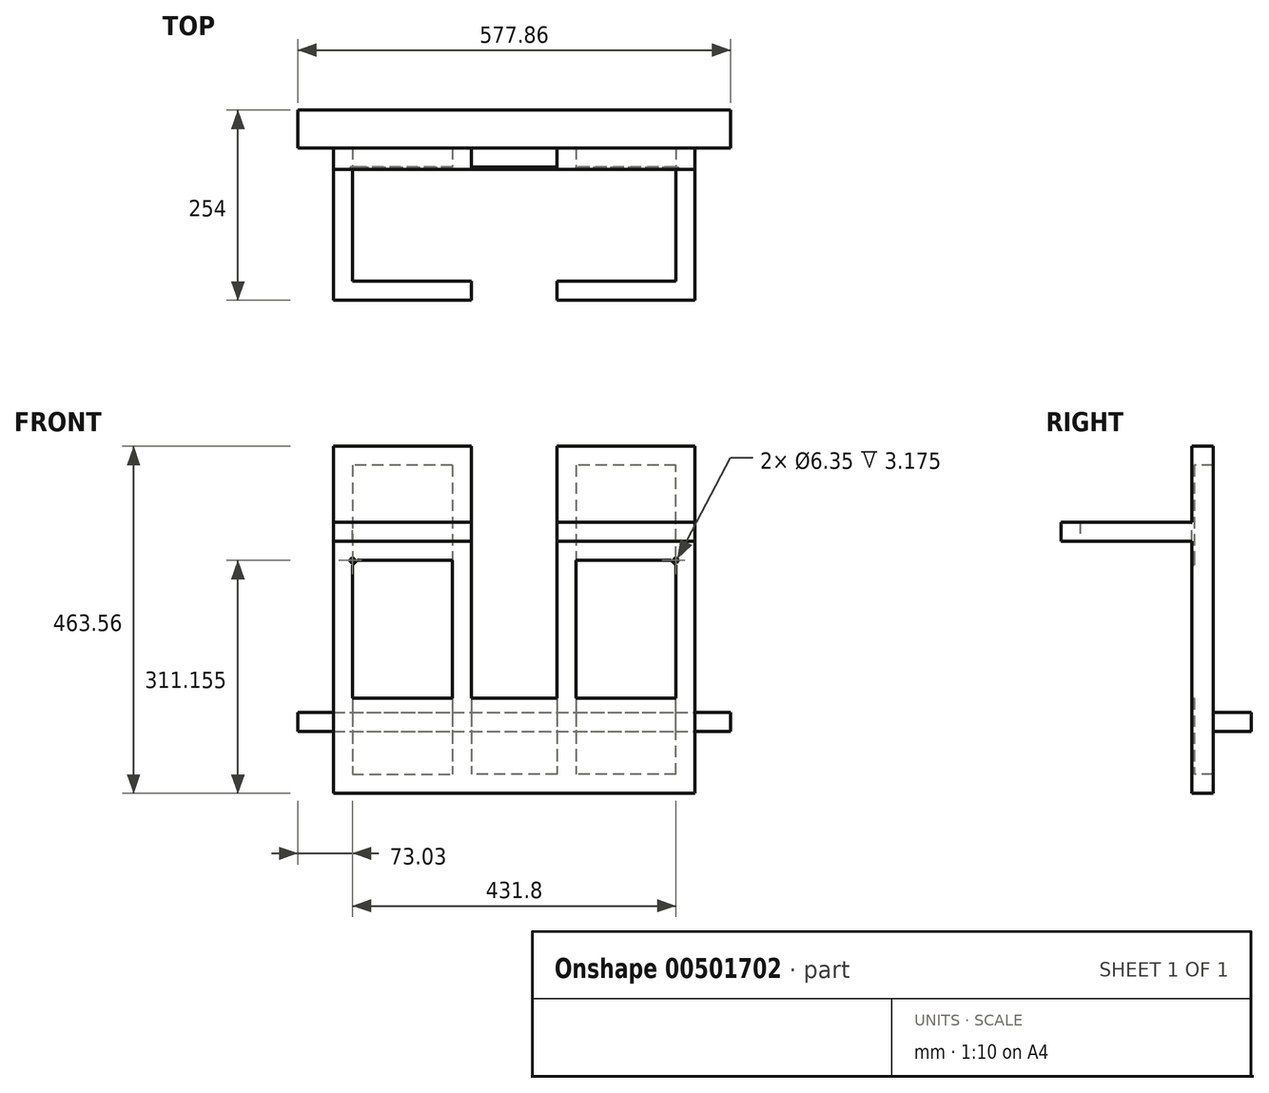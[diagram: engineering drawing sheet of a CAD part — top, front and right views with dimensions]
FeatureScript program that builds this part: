
annotation { "Feature Type Name" : "Feature", "Feature Type Description" : "" }
export const myFeature = defineFeature(function(context is Context, id is Id, definition is map)
    precondition{}
    {
        {
            var Q0;
            Q0=qCreatedBy(makeId("Front.planeOp"),FACE);
            var sketch = newSketch(context, id + "F0", { "sketchPlane" : qUnion([Q0])});
            skLineSegment(sketch, "E0.top", {"start": v(241.3, 231.78) * mm, "end": v(57.15, 231.78) * mm});
            skLineSegment(sketch, "E0.left", {"start": v(241.3, -231.78) * mm, "end": v(241.3, 231.78) * mm});
            skLineSegment(sketch, "E0.right", {"start": v(-241.3, -231.78) * mm, "end": v(-241.3, 231.77) * mm});
            skPoint(sketch, "E0.middle", {"position": v(0, 0) * mm});
            skLineSegment(sketch, "E1", {"start": v(-241.3, 231.77) * mm, "end": v(-57.15, 231.77) * mm});
            skLineSegment(sketch, "E2.trimOffspring", {"start": v(-57.15, 231.78) * mm, "end": v(-241.3, 231.77) * mm});
            skLineSegment(sketch, "E3", {"start": v(-241.3, 231.77) * mm, "end": v(-241.3, 79.37) * mm});
            skLineSegment(sketch, "E4", {"start": v(-209.55, 79.37) * mm, "end": v(-82.55, 79.37) * mm});
            skLineSegment(sketch, "E5", {"start": v(82.55, 79.37) * mm, "end": v(209.55, 79.37) * mm});
            skLineSegment(sketch, "E6", {"start": v(-82.55, 79.37) * mm, "end": v(-82.55, -104.78) * mm});
            skLineSegment(sketch, "E7", {"start": v(-215.9, 73.02) * mm, "end": v(-215.9, -104.78) * mm});
            skLineSegment(sketch, "E8", {"start": v(215.9, -104.78) * mm, "end": v(215.9, 73.02) * mm});
            skLineSegment(sketch, "E9", {"start": v(-241.3, -231.78) * mm, "end": v(241.3, -231.78) * mm});
            skLineSegment(sketch, "E10", {"start": v(-57.15, 231.77) * mm, "end": v(-57.15, -104.78) * mm});
            skLineSegment(sketch, "E11", {"start": v(57.15, 231.78) * mm, "end": v(57.15, -104.78) * mm});
            skLineSegment(sketch, "E12", {"start": v(82.55, -104.78) * mm, "end": v(82.55, 79.37) * mm});
            skLineSegment(sketch, "E13", {"start": v(-241.3, -231.78) * mm, "end": v(-241.3, -104.78) * mm});
            skLineSegment(sketch, "E14", {"start": v(-215.9, -104.78) * mm, "end": v(-82.55, -104.78) * mm});
            skLineSegment(sketch, "E15.trimOffspring", {"start": v(-57.15, -104.78) * mm, "end": v(57.15, -104.78) * mm});
            skLineSegment(sketch, "E16.trimOffspring", {"start": v(82.55, -104.78) * mm, "end": v(215.9, -104.78) * mm});
            skLineSegment(sketch, "E17", {"start": v(-209.55, 79.37) * mm, "end": v(-215.9, 73.02) * mm});
            skLineSegment(sketch, "E18", {"start": v(215.9, 73.02) * mm, "end": v(209.55, 79.37) * mm});
            skSolve(sketch);
        }
        {
            var Q0;
            Q0 = qSketchRegion(id + "F0", true);
            extrude(context, id + "F1", {"entities" : qUnion([Q0]), "depth" : 3.17 * mm});
        }
        {
            var Q0;
            Q0=makeQuery(id+"F1.opExtrude","SWEPT_FACE",FACE,{"disambiguationData":[OSD([sQuery(id+"F0.wireOp",EDGE,"E0.left")])]});
            var sketch = newSketch(context, id + "F2", { "sketchPlane" : qUnion([Q0])});
            skLineSegment(sketch, "E19", {"start": v(0, 130.18) * mm, "end": v(-177.8, 130.18) * mm});
            skLineSegment(sketch, "E20", {"start": v(-177.8, 130.18) * mm, "end": v(-177.8, 104.78) * mm});
            skLineSegment(sketch, "E21", {"start": v(-177.8, 104.78) * mm, "end": v(0, 104.78) * mm});
            skLineSegment(sketch, "E22", {"start": v(0, 104.78) * mm, "end": v(0, 130.18) * mm});
            skSolve(sketch);
        }
        {
            var Q0;
            Q0 = qSketchRegion(id + "F2", true);
            extrude(context, id + "F3", {"entities" : qUnion([Q0]), "operationType" : NewBodyOperationType.ADD, "oppositeDirection" : true, "depth" : 25.4 * mm});
        }
        {
            var Q0;
            Q0=makeQuery(id+"F3.opExtrude","SWEPT_FACE",FACE,{"disambiguationData":[OSD([sQuery(id+"F2.wireOp",EDGE,"E20")])]});
            var sketch = newSketch(context, id + "F4", { "sketchPlane" : qUnion([Q0])});
            skLineSegment(sketch, "E23", {"start": v(241.3, 130.18) * mm, "end": v(57.15, 130.18) * mm});
            skLineSegment(sketch, "E24", {"start": v(57.15, 130.18) * mm, "end": v(57.15, 104.78) * mm});
            skLineSegment(sketch, "E25", {"start": v(57.15, 104.78) * mm, "end": v(241.3, 104.78) * mm});
            skLineSegment(sketch, "E26", {"start": v(241.3, 130.18) * mm, "end": v(241.3, 104.78) * mm});
            skSolve(sketch);
        }
        {
            var Q0;
            Q0 = qSketchRegion(id + "F4", true);
            extrude(context, id + "F5", {"entities" : qUnion([Q0]), "operationType" : NewBodyOperationType.ADD, "oppositeDirection" : true, "depth" : 25.4 * mm});
        }
        {
            var Q0;
            Q0=makeQuery(id+"F1.opExtrude","SWEPT_BODY",BODY,{"disambiguationData":[OSD([sQuery(id+"F0.wireOp",EDGE,"E0.bottom"),sQuery(id+"F0.wireOp",EDGE,"E0.left"),sQuery(id+"F0.wireOp",EDGE,"E0.right"),sQuery(id+"F0.wireOp",EDGE,"E0.top"),sQuery(id+"F0.wireOp",EDGE,"z7k5WuwH-fP3U-BbjL-vrnD-IwZhUuzp3tKr"),sQuery(id+"F0.wireOp",EDGE,"sfKOh3xY-R45W-dPWh-zpq8-PP8cvFYOitUN"),sQuery(id+"F0.wireOp",EDGE,"E2.trimOffspring"),sQuery(id+"F0.wireOp",EDGE,"tUk4NjoC-bmQa-DXwl-oMC2-rkoS1IceVBJg")])]});
            var Q1;
            Q1=qCreatedBy(makeId("Right.planeOp"),FACE);
            mirror(context, id + "F6", {"operationType" : NewBodyOperationType.ADD, "entities" : qUnion([Q0]), "mirrorPlane" : qUnion([Q1])});
        }
        {
            var Q0;
            Q0=makeQuery(id+"F1.opExtrude","CAP_FACE",FACE,{"disambiguationData":[OSD([sQuery(id+"F0.wireOp",EDGE,"E0.bottom"),sQuery(id+"F0.wireOp",EDGE,"E0.left"),sQuery(id+"F0.wireOp",EDGE,"E0.right"),sQuery(id+"F0.wireOp",EDGE,"E0.top"),sQuery(id+"F0.wireOp",EDGE,"z7k5WuwH-fP3U-BbjL-vrnD-IwZhUuzp3tKr"),sQuery(id+"F0.wireOp",EDGE,"sfKOh3xY-R45W-dPWh-zpq8-PP8cvFYOitUN"),sQuery(id+"F0.wireOp",EDGE,"E2.trimOffspring"),sQuery(id+"F0.wireOp",EDGE,"tUk4NjoC-bmQa-DXwl-oMC2-rkoS1IceVBJg")])],"isStart":false});
            var sketch = newSketch(context, id + "F7", { "sketchPlane" : qUnion([Q0])});
            skLineSegment(sketch, "E27.top", {"start": v(107.95, 215.44) * mm, "end": v(-107.95, 215.44) * mm});
            skPoint(sketch, "E27.middle", {"position": v(0, 0) * mm});
            skPoint(sketch, "E27.left.start.orphan", {"position": v(107.95, -215.44) * mm});
            skPoint(sketch, "E27.right.start.orphan", {"position": v(-107.95, -215.44) * mm});
            skCircle(sketch, "E28", {"center": v(-215.9, 79.38) * mm, "radius": 3.18 * mm});
            skCircle(sketch, "E29.MirrorC", {"center": v(215.9, 79.38) * mm, "radius": 3.18 * mm});
            skSolve(sketch);
        }
        {
            var Q0;
            Q0 = qSketchRegion(id + "F7", true);
            extrude(context, id + "F8", {"entities" : qUnion([Q0]), "operationType" : NewBodyOperationType.REMOVE, "oppositeDirection" : true, "depth" : 25.4 * mm});
        }
        {
            var Q0;
            Q0=makeQuery(id+"F1.opExtrude","CAP_FACE",FACE,{"disambiguationData":[OSD([sQuery(id+"F0.wireOp",EDGE,"E0.bottom"),sQuery(id+"F0.wireOp",EDGE,"E0.left"),sQuery(id+"F0.wireOp",EDGE,"E0.right"),sQuery(id+"F0.wireOp",EDGE,"E0.top"),sQuery(id+"F0.wireOp",EDGE,"z7k5WuwH-fP3U-BbjL-vrnD-IwZhUuzp3tKr"),sQuery(id+"F0.wireOp",EDGE,"sfKOh3xY-R45W-dPWh-zpq8-PP8cvFYOitUN"),sQuery(id+"F0.wireOp",EDGE,"E2.trimOffspring"),sQuery(id+"F0.wireOp",EDGE,"tUk4NjoC-bmQa-DXwl-oMC2-rkoS1IceVBJg")])],"isStart":true});
            var sketch = newSketch(context, id + "F9", { "sketchPlane" : qUnion([Q0])});
            skLineSegment(sketch, "E30", {"start": v(-241.3, 231.78) * mm, "end": v(-241.3, 231.78) * mm});
            skLineSegment(sketch, "E31", {"start": v(-241.3, 231.78) * mm, "end": v(-241.3, -206.38) * mm});
            skLineSegment(sketch, "E32", {"start": v(-241.3, -231.78) * mm, "end": v(-241.3, 231.78) * mm});
            skLineSegment(sketch, "E33", {"start": v(-215.9, 206.38) * mm, "end": v(-82.55, 206.38) * mm});
            skLineSegment(sketch, "E34", {"start": v(-215.9, -206.38) * mm, "end": v(-215.9, 206.38) * mm});
            skLineSegment(sketch, "E35", {"start": v(-215.9, -206.38) * mm, "end": v(-82.55, -206.38) * mm});
            skLineSegment(sketch, "E36", {"start": v(82.55, 206.37) * mm, "end": v(82.55, -206.38) * mm});
            skLineSegment(sketch, "E37", {"start": v(57.15, 231.78) * mm, "end": v(57.15, 231.78) * mm});
            skLineSegment(sketch, "E38", {"start": v(241.3, -231.78) * mm, "end": v(241.3, 231.77) * mm});
            skLineSegment(sketch, "E39", {"start": v(241.3, 231.77) * mm, "end": v(57.15, 231.77) * mm});
            skLineSegment(sketch, "E40", {"start": v(-241.3, 231.78) * mm, "end": v(-57.15, 231.78) * mm});
            skLineSegment(sketch, "E41", {"start": v(-57.15, 231.78) * mm, "end": v(-57.15, -206.38) * mm});
            skLineSegment(sketch, "E42", {"start": v(82.55, 206.37) * mm, "end": v(215.9, 206.37) * mm});
            skLineSegment(sketch, "E43", {"start": v(215.9, 206.37) * mm, "end": v(215.9, -206.38) * mm});
            skLineSegment(sketch, "E44", {"start": v(215.9, -206.38) * mm, "end": v(82.55, -206.38) * mm});
            skLineSegment(sketch, "E45", {"start": v(241.3, -231.78) * mm, "end": v(-241.3, -231.78) * mm});
            skLineSegment(sketch, "E46", {"start": v(-57.15, -206.38) * mm, "end": v(57.15, -206.38) * mm});
            skLineSegment(sketch, "E47", {"start": v(57.15, 231.78) * mm, "end": v(57.15, -206.38) * mm});
            skLineSegment(sketch, "E48", {"start": v(-82.55, 206.38) * mm, "end": v(-82.55, -206.38) * mm});
            skSolve(sketch);
        }
        {
            var Q0;
            Q0 = qSketchRegion(id + "F9", true);
            extrude(context, id + "F10", {"entities" : qUnion([Q0]), "operationType" : NewBodyOperationType.ADD, "depth" : 25.4 * mm});
        }
        {
            var Q0;
            Q0=makeQuery(id+"F10.boolean.opBoolean","MERGE",FACE,{"derivedFrom":[makeQuery(id+"F3.boolean.opBoolean","MERGE",FACE,{"derivedFrom":[makeQuery(id+"F1.opExtrude","SWEPT_FACE",FACE,{"disambiguationData":[OSD([sQuery(id+"F0.wireOp",EDGE,"E0.left")])]}),makeQuery(id+"F3.opExtrude","CAP_FACE",FACE,{"disambiguationData":[OSD([sQuery(id+"F2.wireOp",EDGE,"E19"),sQuery(id+"F2.wireOp",EDGE,"E20"),sQuery(id+"F2.wireOp",EDGE,"E21"),sQuery(id+"F2.wireOp",EDGE,"E22")])],"isStart":true})]}),makeQuery(id+"F10.opExtrude","SWEPT_FACE",FACE,{"disambiguationData":[OSD([sQuery(id+"F9.wireOp",EDGE,"E32")])]})]});
            var sketch = newSketch(context, id + "F11", { "sketchPlane" : qUnion([Q0])});
            skLineSegment(sketch, "E49", {"start": v(25.4, -149.22) * mm, "end": v(76.2, -149.22) * mm});
            skLineSegment(sketch, "E50", {"start": v(76.2, -149.22) * mm, "end": v(76.2, -123.82) * mm});
            skLineSegment(sketch, "E51", {"start": v(76.2, -123.82) * mm, "end": v(25.4, -123.82) * mm});
            skLineSegment(sketch, "E52", {"start": v(25.4, -123.82) * mm, "end": v(25.4, -149.22) * mm});
            skSolve(sketch);
        }
        {
            var Q0;
            Q0 = qSketchRegion(id + "F11", true);
            extrude(context, id + "F12", {"entities" : qUnion([Q0]), "operationType" : NewBodyOperationType.ADD, "oppositeDirection" : true, "depth" : 530.23 * mm});
        }
        {
            var Q0;
            Q0=makeQuery(id+"F12.boolean.opBoolean","MERGE",FACE,{"derivedFrom":[makeQuery(id+"F10.boolean.opBoolean","MERGE",FACE,{"derivedFrom":[makeQuery(id+"F3.boolean.opBoolean","MERGE",FACE,{"derivedFrom":[makeQuery(id+"F1.opExtrude","SWEPT_FACE",FACE,{"disambiguationData":[OSD([sQuery(id+"F0.wireOp",EDGE,"E0.left")])]}),makeQuery(id+"F3.opExtrude","CAP_FACE",FACE,{"disambiguationData":[OSD([sQuery(id+"F2.wireOp",EDGE,"E19"),sQuery(id+"F2.wireOp",EDGE,"E20"),sQuery(id+"F2.wireOp",EDGE,"E21"),sQuery(id+"F2.wireOp",EDGE,"E22")])],"isStart":true})]}),makeQuery(id+"F10.opExtrude","SWEPT_FACE",FACE,{"disambiguationData":[OSD([sQuery(id+"F9.wireOp",EDGE,"E32")])]})]}),makeQuery(id+"F12.opExtrude","CAP_FACE",FACE,{"disambiguationData":[OSD([sQuery(id+"F11.wireOp",EDGE,"E49"),sQuery(id+"F11.wireOp",EDGE,"E50"),sQuery(id+"F11.wireOp",EDGE,"E51"),sQuery(id+"F11.wireOp",EDGE,"E52")])],"isStart":true})]});
            var sketch = newSketch(context, id + "F13", { "sketchPlane" : qUnion([Q0])});
            skLineSegment(sketch, "E53", {"start": v(76.2, -123.82) * mm, "end": v(76.2, -149.22) * mm});
            skLineSegment(sketch, "E54", {"start": v(76.2, -149.22) * mm, "end": v(25.4, -149.22) * mm});
            skLineSegment(sketch, "E55", {"start": v(25.4, -149.22) * mm, "end": v(25.4, -123.82) * mm});
            skLineSegment(sketch, "E56", {"start": v(25.4, -123.82) * mm, "end": v(76.2, -123.82) * mm});
            skSolve(sketch);
        }
        {
            var Q0;
            Q0 = qSketchRegion(id + "F13", true);
            extrude(context, id + "F14", {"entities" : qUnion([Q0]), "operationType" : NewBodyOperationType.ADD, "depth" : 47.62 * mm});
        }
    });
